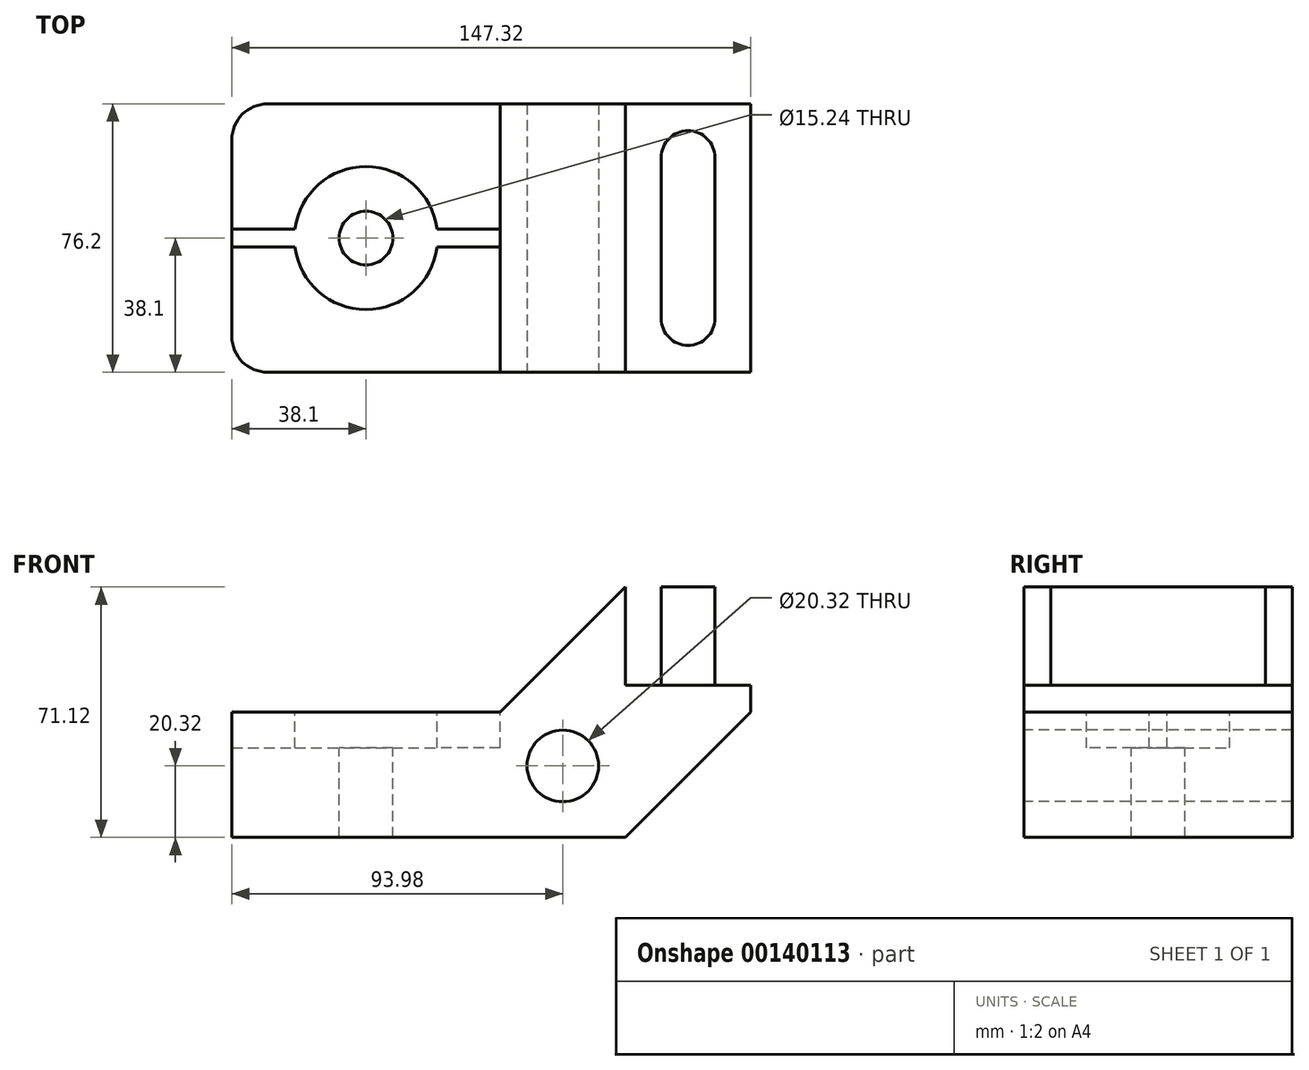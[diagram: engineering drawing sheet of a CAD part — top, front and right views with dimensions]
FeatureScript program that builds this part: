
annotation { "Feature Type Name" : "Feature", "Feature Type Description" : "" }
export const myFeature = defineFeature(function(context is Context, id is Id, definition is map)
    precondition{}
    {
        {
            var Q0;
            Q0=qCreatedBy(makeId("Front.planeOp"),FACE);
            var sketch = newSketch(context, id + "F0", { "sketchPlane" : qUnion([Q0])});
            skLineSegment(sketch, "E0", {"start": v(0, 0) * mm, "end": v(111.76, 0) * mm});
            skLineSegment(sketch, "E1", {"start": v(111.76, 0) * mm, "end": v(147.32, 35.56) * mm});
            skLineSegment(sketch, "E2", {"start": v(147.32, 35.56) * mm, "end": v(147.32, 71.12) * mm});
            skLineSegment(sketch, "E3", {"start": v(147.32, 71.12) * mm, "end": v(111.76, 71.12) * mm});
            skLineSegment(sketch, "E4", {"start": v(111.76, 71.12) * mm, "end": v(76.2, 35.56) * mm});
            skLineSegment(sketch, "E5", {"start": v(76.2, 35.56) * mm, "end": v(0, 35.56) * mm});
            skLineSegment(sketch, "E6", {"start": v(0, 35.56) * mm, "end": v(0, 0) * mm});
            skSolve(sketch);
        }
        {
            var Q0;
            Q0=makeQuery(id+"F0.imprint","IMPRINT",FACE,{"disambiguationData":[TD([[makeQuery(id+"F0.imprint","IMPRINT",EDGE,{"derivedFrom":sQuery(id+"F0.wireOp",EDGE,"E0")}),1.0]])]});
            extrude(context, id + "F1", {"entities" : qUnion([Q0]), "oppositeDirection" : true, "depth" : 76.2 * mm});
        }
        {
            var Q0;
            Q0=makeQuery(id+"F1.opExtrude","CAP_FACE",FACE,{"disambiguationData":[OSD([sQuery(id+"F0.wireOp",EDGE,"E0"),sQuery(id+"F0.wireOp",EDGE,"E1"),sQuery(id+"F0.wireOp",EDGE,"E2"),sQuery(id+"F0.wireOp",EDGE,"E3"),sQuery(id+"F0.wireOp",EDGE,"E4"),sQuery(id+"F0.wireOp",EDGE,"E5"),sQuery(id+"F0.wireOp",EDGE,"E6")])],"isStart":true});
            var sketch = newSketch(context, id + "F2", { "sketchPlane" : qUnion([Q0])});
            skLineSegment(sketch, "E7", {"start": v(0, 0) * mm, "end": v(0, 20.32) * mm, "construction": true});
            skLineSegment(sketch, "E8", {"start": v(0, 20.32) * mm, "end": v(93.98, 20.32) * mm, "construction": true});
            skSolve(sketch);
        }
        {
            var Q0;
            Q0=sQuery(id+"F2.wireOp",VERTEX,"E8.end");
            var Q1;
            Q1=makeQuery(id+"F1.opExtrude","SWEPT_BODY",BODY,{"disambiguationData":[OSD([sQuery(id+"F0.wireOp",EDGE,"E0"),sQuery(id+"F0.wireOp",EDGE,"E1"),sQuery(id+"F0.wireOp",EDGE,"E2"),sQuery(id+"F0.wireOp",EDGE,"E3"),sQuery(id+"F0.wireOp",EDGE,"E4"),sQuery(id+"F0.wireOp",EDGE,"E5"),sQuery(id+"F0.wireOp",EDGE,"E6")])]});
            hole(context, id + "F3", {"style" : HoleStyle.SIMPLE, "endStyle" : HoleEndStyle.THROUGH, "holeDiameter" : 20.32 * mm, "locations" : qUnion([Q0]), "scope" : qUnion([Q1]), "isTappedThrough" : true});
        }
        {
            var Q0;
            Q0=makeQuery(id+"F1.opExtrude","SWEPT_FACE",FACE,{"disambiguationData":[OSD([sQuery(id+"F0.wireOp",EDGE,"E3")])]});
            var sketch = newSketch(context, id + "F4", { "sketchPlane" : qUnion([Q0])});
            skLineSegment(sketch, "E9", {"start": v(147.32, 76.2) * mm, "end": v(147.32, 60.96) * mm, "construction": true});
            skLineSegment(sketch, "E10", {"start": v(147.32, 60.96) * mm, "end": v(129.54, 60.96) * mm, "construction": true});
            skLineSegment(sketch, "E11", {"start": v(129.54, 60.96) * mm, "end": v(129.54, 15.24) * mm, "construction": true});
            skArc(sketch, "E12", {"start": v(121.92, 60.96) * mm, "mid": v(129.54, 68.58) * mm, "end": v(137.16, 60.96) * mm});
            skArc(sketch, "E13", {"start": v(121.92, 15.24) * mm, "mid": v(129.54, 7.62) * mm, "end": v(137.16, 15.24) * mm});
            skLineSegment(sketch, "E14", {"start": v(121.92, 60.96) * mm, "end": v(121.92, 15.24) * mm});
            skLineSegment(sketch, "E15", {"start": v(137.16, 60.96) * mm, "end": v(137.16, 15.24) * mm});
            skSolve(sketch);
        }
        {
            var Q0;
            Q0=makeQuery(id+"F4.imprint","IMPRINT",FACE,{"disambiguationData":[TD([[makeQuery(id+"F4.imprint","IMPRINT",EDGE,{"derivedFrom":sQuery(id+"F4.wireOp",EDGE,"E12")}),-1.0]])]});
            extrude(context, id + "F5", {"entities" : qUnion([Q0]), "operationType" : NewBodyOperationType.REMOVE, "oppositeDirection" : true, "depth" : 27.94 * mm});
        }
        {
            var Q0;
            Q0=makeQuery(id+"F1.opExtrude","SWEPT_FACE",FACE,{"disambiguationData":[OSD([sQuery(id+"F0.wireOp",EDGE,"E5")])]});
            var sketch = newSketch(context, id + "F6", { "sketchPlane" : qUnion([Q0])});
            skLineSegment(sketch, "E16", {"start": v(38.1, 76.2) * mm, "end": v(38.1, 38.1) * mm, "construction": true});
            skPoint(sketch, "E16.endSnap0", {"position": v(0, 38.1) * mm});
            skSolve(sketch);
        }
        {
            var Q0;
            Q0=sQuery(id+"F6.wireOp",VERTEX,"E16.end");
            var Q1;
            Q1=makeQuery(id+"F1.opExtrude","SWEPT_BODY",BODY,{"disambiguationData":[OSD([sQuery(id+"F0.wireOp",EDGE,"E0"),sQuery(id+"F0.wireOp",EDGE,"E1"),sQuery(id+"F0.wireOp",EDGE,"E2"),sQuery(id+"F0.wireOp",EDGE,"E3"),sQuery(id+"F0.wireOp",EDGE,"E4"),sQuery(id+"F0.wireOp",EDGE,"E5"),sQuery(id+"F0.wireOp",EDGE,"E6")])]});
            hole(context, id + "F7", {"style" : HoleStyle.C_BORE, "endStyle" : HoleEndStyle.THROUGH, "holeDiameter" : 15.24 * mm, "cBoreDiameter" : 40.64 * mm, "cBoreDepth" : 10.16 * mm, "locations" : qUnion([Q0]), "scope" : qUnion([Q1]), "isTappedThrough" : true});
        }
        {
            var Q0;
            Q0=makeQuery(id+"F1.opExtrude","SWEPT_FACE",FACE,{"disambiguationData":[OSD([sQuery(id+"F0.wireOp",EDGE,"E5")])]});
            var sketch = newSketch(context, id + "F8", { "sketchPlane" : qUnion([Q0])});
            skLineSegment(sketch, "E17", {"start": v(0, 38.1) * mm, "end": v(0, 40.64) * mm});
            skLineSegment(sketch, "E18", {"start": v(0, 40.64) * mm, "end": v(17.94, 40.64) * mm});
            skLineSegment(sketch, "E19", {"start": v(0, 38.1) * mm, "end": v(0, 35.56) * mm});
            skLineSegment(sketch, "E20", {"start": v(0, 35.56) * mm, "end": v(17.94, 35.56) * mm});
            skLineSegment(sketch, "E21.MirrorCS", {"start": v(76.2, 40.64) * mm, "end": v(58.26, 40.64) * mm});
            skLineSegment(sketch, "E22.MirrorCS", {"start": v(76.2, 35.56) * mm, "end": v(58.26, 35.56) * mm});
            skLineSegment(sketch, "E23.MirrorCS", {"start": v(76.2, 38.1) * mm, "end": v(76.2, 35.56) * mm});
            skLineSegment(sketch, "E24.MirrorCS", {"start": v(76.2, 38.1) * mm, "end": v(76.2, 40.64) * mm});
            skSolve(sketch);
        }
        {
            var Q0;
            Q0=makeQuery(id+"F8.imprint","IMPRINT",FACE,{"disambiguationData":[TD([[makeQuery(id+"F8.imprint","IMPRINT",EDGE,{"derivedFrom":sQuery(id+"F8.wireOp",EDGE,"E17")}),1.0]])]});
            var Q1;
            {var subQ1=sQuery(id+"F8.wireOp",EDGE,"E21.MirrorCS");Q1=makeQuery(id+"F8.imprint","IMPRINT",FACE,{"disambiguationData":[TD([[makeQuery(id+"F8.imprint","IMPRINT",EDGE,{"derivedFrom":subQ1}),1.0]])]});}
            extrude(context, id + "F9", {"entities" : qUnion([Q0, Q1]), "operationType" : NewBodyOperationType.REMOVE, "oppositeDirection" : true, "depth" : 10.16 * mm});
        }
        {
            var Q0;
            Q0=makeQuery(id+"F1.opExtrude","CAP_EDGE",EDGE,{"disambiguationData":[OSD([sQuery(id+"F0.wireOp",EDGE,"E6")])],"isStart":false});
            var Q1;
            Q1=makeQuery(id+"F1.opExtrude","CAP_EDGE",EDGE,{"disambiguationData":[OSD([sQuery(id+"F0.wireOp",EDGE,"E6")])],"isStart":true});
            fillet(context, id + "F10", {"entities" : qUnion([Q0, Q1]), "radius" : 10.16 * mm, "tangentPropagation" : true, "allowEdgeOverflow" : false});
        }
    });
